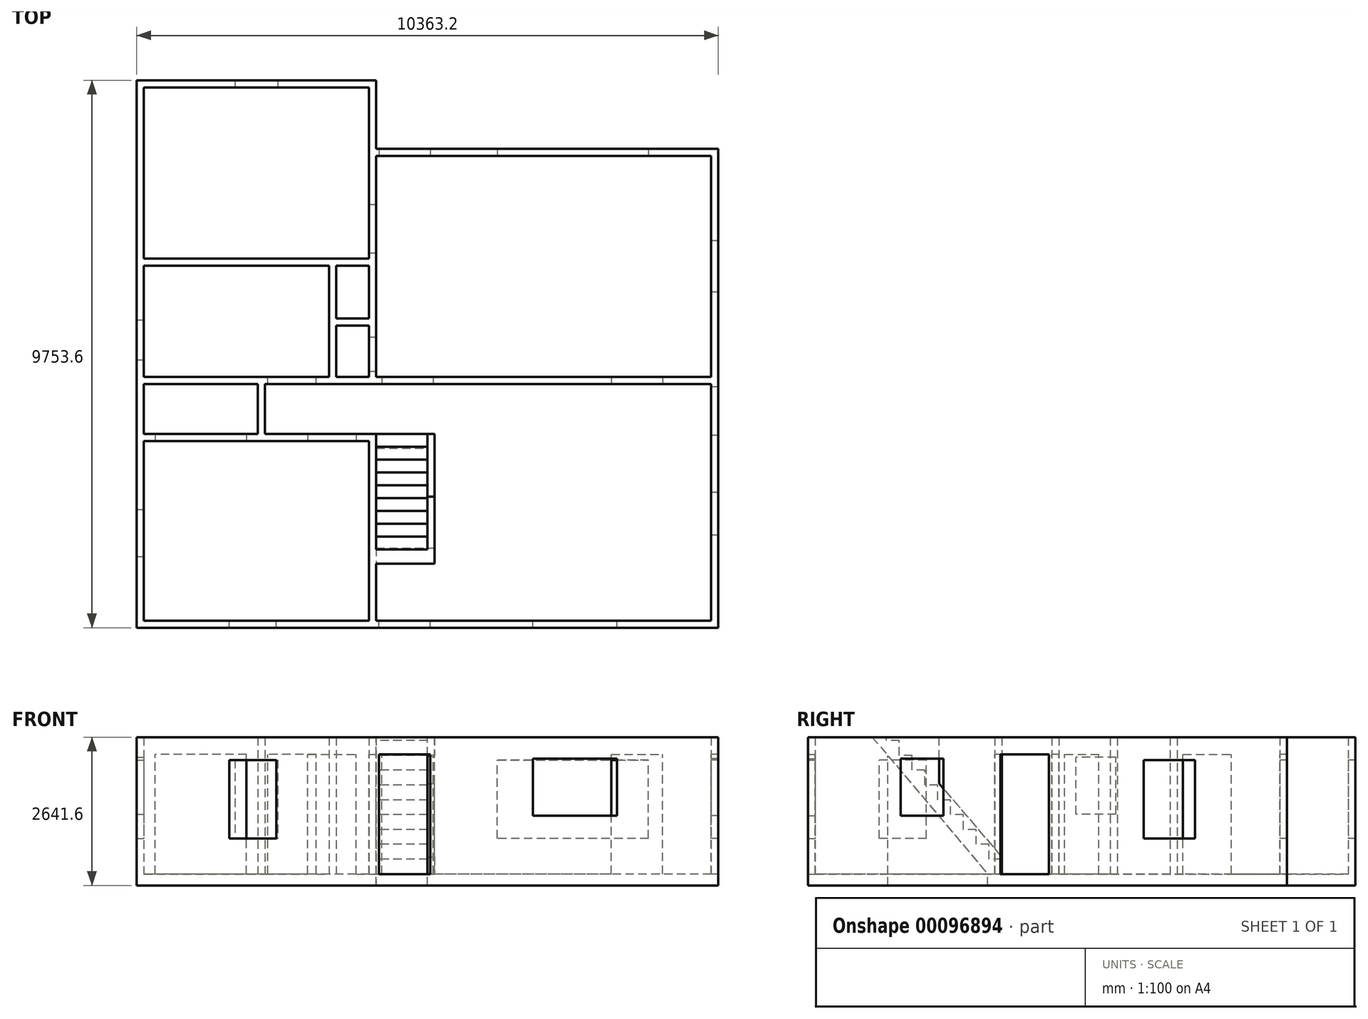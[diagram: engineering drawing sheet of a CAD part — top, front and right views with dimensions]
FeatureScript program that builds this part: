
annotation { "Feature Type Name" : "Feature", "Feature Type Description" : "" }
export const myFeature = defineFeature(function(context is Context, id is Id, definition is map)
    precondition{}
    {
        {
            var Q0;
            Q0=qCreatedBy(makeId("Top.planeOp"),FACE);
            var sketch = newSketch(context, id + "F0", { "sketchPlane" : qUnion([Q0])});
            skLineSegment(sketch, "E0", {"start": v(0, 0) * mm, "end": v(10363.2, 0) * mm});
            skLineSegment(sketch, "E1", {"start": v(10363.2, 0) * mm, "end": v(10363.2, 8534.4) * mm});
            skLineSegment(sketch, "E2", {"start": v(10363.2, 8534.4) * mm, "end": v(4267.2, 8534.4) * mm});
            skLineSegment(sketch, "E3", {"start": v(4267.2, 8534.4) * mm, "end": v(4267.2, 9753.6) * mm});
            skLineSegment(sketch, "E4", {"start": v(4267.2, 9753.6) * mm, "end": v(0, 9753.6) * mm});
            skLineSegment(sketch, "E5", {"start": v(0, 9753.6) * mm, "end": v(0, 0) * mm});
            skLineSegment(sketch, "E6", {"start": v(127, 3327.4) * mm, "end": v(127, 127) * mm});
            skLineSegment(sketch, "E7", {"start": v(127, 127) * mm, "end": v(4140.2, 127) * mm});
            skLineSegment(sketch, "E8", {"start": v(4140.2, 127) * mm, "end": v(4140.2, 3327.4) * mm});
            skLineSegment(sketch, "E9", {"start": v(4140.2, 3327.4) * mm, "end": v(127, 3327.4) * mm});
            skLineSegment(sketch, "E10", {"start": v(4267.2, 3327.4) * mm, "end": v(4267.2, 127) * mm});
            skLineSegment(sketch, "E11", {"start": v(4267.2, 127) * mm, "end": v(5181.6, 127) * mm});
            skLineSegment(sketch, "E12", {"start": v(5181.6, 127) * mm, "end": v(5181.6, 3327.4) * mm});
            skLineSegment(sketch, "E13", {"start": v(5181.6, 3327.4) * mm, "end": v(4267.2, 3327.4) * mm});
            skLineSegment(sketch, "E14", {"start": v(2286, 3454.4) * mm, "end": v(5308.6, 3454.4) * mm});
            skLineSegment(sketch, "E15", {"start": v(5308.6, 3454.4) * mm, "end": v(5308.6, 127) * mm});
            skLineSegment(sketch, "E16", {"start": v(5308.6, 127) * mm, "end": v(10236.2, 127) * mm});
            skLineSegment(sketch, "E17", {"start": v(10236.2, 127) * mm, "end": v(10236.2, 4343.4) * mm});
            skLineSegment(sketch, "E18", {"start": v(10236.2, 4343.4) * mm, "end": v(2286, 4343.4) * mm});
            skLineSegment(sketch, "E19", {"start": v(2286, 4343.4) * mm, "end": v(2286, 3454.4) * mm});
            skLineSegment(sketch, "E20", {"start": v(4267.2, 8407.4) * mm, "end": v(4267.2, 4470.4) * mm});
            skLineSegment(sketch, "E21", {"start": v(4267.2, 4470.4) * mm, "end": v(10236.2, 4470.4) * mm});
            skLineSegment(sketch, "E22", {"start": v(10236.2, 4470.4) * mm, "end": v(10236.2, 8407.4) * mm});
            skLineSegment(sketch, "E23", {"start": v(10236.2, 8407.4) * mm, "end": v(4267.2, 8407.4) * mm});
            skLineSegment(sketch, "E24", {"start": v(127, 4343.4) * mm, "end": v(127, 3454.4) * mm});
            skLineSegment(sketch, "E25", {"start": v(127, 3454.4) * mm, "end": v(2159, 3454.4) * mm});
            skLineSegment(sketch, "E26", {"start": v(2159, 3454.4) * mm, "end": v(2159, 4343.4) * mm});
            skLineSegment(sketch, "E27", {"start": v(2159, 4343.4) * mm, "end": v(127, 4343.4) * mm});
            skLineSegment(sketch, "E28", {"start": v(127, 6451.6) * mm, "end": v(127, 4470.4) * mm});
            skLineSegment(sketch, "E29", {"start": v(127, 4470.4) * mm, "end": v(3429, 4470.4) * mm});
            skLineSegment(sketch, "E30", {"start": v(3429, 4470.4) * mm, "end": v(3429, 6451.6) * mm});
            skLineSegment(sketch, "E31", {"start": v(3429, 6451.6) * mm, "end": v(127, 6451.6) * mm});
            skLineSegment(sketch, "E32", {"start": v(127, 9626.6) * mm, "end": v(127, 6578.6) * mm});
            skLineSegment(sketch, "E33", {"start": v(127, 6578.6) * mm, "end": v(4140.2, 6578.6) * mm});
            skLineSegment(sketch, "E34", {"start": v(4140.2, 6578.6) * mm, "end": v(4140.2, 9626.6) * mm});
            skLineSegment(sketch, "E35", {"start": v(4140.2, 9626.6) * mm, "end": v(127, 9626.6) * mm});
            skLineSegment(sketch, "E36", {"start": v(3556, 6451.6) * mm, "end": v(3556, 5511.8) * mm});
            skLineSegment(sketch, "E37", {"start": v(3556, 5511.8) * mm, "end": v(4140.2, 5511.8) * mm});
            skLineSegment(sketch, "E38", {"start": v(4140.2, 5511.8) * mm, "end": v(4140.2, 6451.6) * mm});
            skLineSegment(sketch, "E39", {"start": v(4140.2, 6451.6) * mm, "end": v(3556, 6451.6) * mm});
            skLineSegment(sketch, "E40", {"start": v(3556, 5384.8) * mm, "end": v(3556, 4470.4) * mm});
            skLineSegment(sketch, "E41", {"start": v(3556, 4470.4) * mm, "end": v(4140.2, 4470.4) * mm});
            skLineSegment(sketch, "E42", {"start": v(4140.2, 4470.4) * mm, "end": v(4140.2, 5384.8) * mm});
            skLineSegment(sketch, "E43", {"start": v(4140.2, 5384.8) * mm, "end": v(3556, 5384.8) * mm});
            skSolve(sketch);
        }
        {
            var Q0;
            Q0=makeQuery(id+"F0.imprint","IMPRINT",FACE,{"disambiguationData":[TD([[makeQuery(id+"F0.imprint","IMPRINT",EDGE,{"derivedFrom":sQuery(id+"F0.wireOp",EDGE,"E0")}),1.0]])]});
            extrude(context, id + "F1", {"entities" : qUnion([Q0]), "depth" : 2438.4 * mm});
        }
        {
            var Q0;
            Q0=qCreatedBy(makeId("Top.planeOp"),FACE);
            var sketch = newSketch(context, id + "F2", { "sketchPlane" : qUnion([Q0])});
            skLineSegment(sketch, "E44", {"start": v(0, 0) * mm, "end": v(10363.2, 0) * mm});
            skLineSegment(sketch, "E45", {"start": v(10363.2, 0) * mm, "end": v(10363.2, 8534.4) * mm});
            skLineSegment(sketch, "E46", {"start": v(10363.2, 8534.4) * mm, "end": v(4267.2, 8534.4) * mm});
            skLineSegment(sketch, "E47", {"start": v(4267.2, 8534.4) * mm, "end": v(4267.2, 9753.6) * mm});
            skLineSegment(sketch, "E48", {"start": v(4267.2, 9753.6) * mm, "end": v(0, 9753.6) * mm});
            skLineSegment(sketch, "E49", {"start": v(0, 9753.6) * mm, "end": v(0, 0) * mm});
            skLineSegment(sketch, "E50.bottom", {"start": v(4267.2, 3200.4) * mm, "end": v(5181.6, 3200.4) * mm});
            skLineSegment(sketch, "E50.top", {"start": v(4267.2, 1422.4) * mm, "end": v(5181.6, 1422.4) * mm});
            skLineSegment(sketch, "E50.left", {"start": v(4267.2, 3200.4) * mm, "end": v(4267.2, 1422.4) * mm});
            skLineSegment(sketch, "E50.right", {"start": v(5181.6, 3200.4) * mm, "end": v(5181.6, 1422.4) * mm});
            skSolve(sketch);
        }
        {
            var Q0;
            Q0=makeQuery(id+"F2.imprint","IMPRINT",FACE,{"disambiguationData":[TD([[makeQuery(id+"F2.imprint","IMPRINT",EDGE,{"derivedFrom":sQuery(id+"F2.wireOp",EDGE,"E44")}),1.0]])]});
            extrude(context, id + "F3", {"entities" : qUnion([Q0]), "operationType" : NewBodyOperationType.ADD, "oppositeDirection" : true, "depth" : 203.2 * mm});
        }
        {
            var Q0;
            Q0=makeQuery(id+"F1.opExtrude","SWEPT_FACE",FACE,{"disambiguationData":[OSD([sQuery(id+"F0.wireOp",EDGE,"E17")])]});
            var sketch = newSketch(context, id + "F4", { "sketchPlane" : qUnion([Q0])});
            skLineSegment(sketch, "E51.bottom", {"start": v(-4292.6, 0) * mm, "end": v(-3429, 0) * mm});
            skLineSegment(sketch, "E51.top", {"start": v(-4292.6, 2133.6) * mm, "end": v(-3429, 2133.6) * mm});
            skLineSegment(sketch, "E51.left", {"start": v(-4292.6, 0) * mm, "end": v(-4292.6, 2133.6) * mm});
            skLineSegment(sketch, "E51.right", {"start": v(-3429, 0) * mm, "end": v(-3429, 2133.6) * mm});
            skLineSegment(sketch, "E52.bottom", {"start": v(-2413, 2057.4) * mm, "end": v(-1651, 2057.4) * mm});
            skLineSegment(sketch, "E52.top", {"start": v(-2413, 1041.4) * mm, "end": v(-1651, 1041.4) * mm});
            skLineSegment(sketch, "E52.left", {"start": v(-2413, 2057.4) * mm, "end": v(-2413, 1041.4) * mm});
            skLineSegment(sketch, "E52.right", {"start": v(-1651, 2057.4) * mm, "end": v(-1651, 1041.4) * mm});
            skSolve(sketch);
        }
        {
            var Q0;
            Q0 = qSketchRegion(id + "F4", true);
            extrude(context, id + "F5", {"entities" : qUnion([Q0]), "operationType" : NewBodyOperationType.REMOVE, "endBound" : BoundingType.UP_TO_NEXT, "oppositeDirection" : true, "depth" : 25.4 * mm});
        }
        {
            var Q0;
            Q0=makeQuery(id+"F1.opExtrude","SWEPT_FACE",FACE,{"disambiguationData":[OSD([sQuery(id+"F0.wireOp",EDGE,"E18")])]});
            var sketch = newSketch(context, id + "F6", { "sketchPlane" : qUnion([Q0])});
            skLineSegment(sketch, "E53.bottom", {"start": v(4368.8, 0) * mm, "end": v(5283.2, 0) * mm});
            skLineSegment(sketch, "E53.top", {"start": v(4368.8, 2133.6) * mm, "end": v(5283.2, 2133.6) * mm});
            skLineSegment(sketch, "E53.left", {"start": v(5283.2, 0) * mm, "end": v(5283.2, 2133.6) * mm});
            skLineSegment(sketch, "E53.right", {"start": v(4368.8, 0) * mm, "end": v(4368.8, 2133.6) * mm});
            skLineSegment(sketch, "E54.bottom", {"start": v(8458.2, 0) * mm, "end": v(9372.6, 0) * mm});
            skLineSegment(sketch, "E54.top", {"start": v(8458.2, 2133.6) * mm, "end": v(9372.6, 2133.6) * mm});
            skLineSegment(sketch, "E54.left", {"start": v(8458.2, 0) * mm, "end": v(8458.2, 2133.6) * mm});
            skLineSegment(sketch, "E54.right", {"start": v(9372.6, 0) * mm, "end": v(9372.6, 2133.6) * mm});
            skSolve(sketch);
        }
        {
            var Q0;
            Q0 = qSketchRegion(id + "F6", true);
            extrude(context, id + "F7", {"entities" : qUnion([Q0]), "operationType" : NewBodyOperationType.REMOVE, "endBound" : BoundingType.UP_TO_NEXT, "oppositeDirection" : true, "depth" : 25.4 * mm});
        }
        {
            var Q0;
            Q0=makeQuery(id+"F1.opExtrude","SWEPT_FACE",FACE,{"disambiguationData":[OSD([sQuery(id+"F0.wireOp",EDGE,"E15")])]});
            var sketch = newSketch(context, id + "F8", { "sketchPlane" : qUnion([Q0])});
            skLineSegment(sketch, "E55.bottom", {"start": v(127, 0) * mm, "end": v(1422.4, 0) * mm});
            skLineSegment(sketch, "E55.left", {"start": v(127, 0) * mm, "end": v(127, 2438.4) * mm});
            skLineSegment(sketch, "E55.right", {"start": v(1422.4, 0) * mm, "end": v(1422.4, 2107.26) * mm});
            skLineSegment(sketch, "E56", {"start": v(1143, 2438.4) * mm, "end": v(127, 2438.4) * mm});
            skLineSegment(sketch, "E57", {"start": v(1143, 2438.4) * mm, "end": v(1422.4, 2107.26) * mm});
            skSolve(sketch);
        }
        {
            var Q0;
            Q0 = qSketchRegion(id + "F8", true);
            extrude(context, id + "F9", {"entities" : qUnion([Q0]), "operationType" : NewBodyOperationType.REMOVE, "endBound" : BoundingType.UP_TO_NEXT, "oppositeDirection" : true, "depth" : 25.4 * mm});
        }
        {
            var Q0;
            Q0=makeQuery(id+"F9.boolean.opBoolean","MERGE",FACE,{"derivedFrom":[makeQuery(id+"F1.opExtrude","SWEPT_FACE",FACE,{"disambiguationData":[OSD([sQuery(id+"F0.wireOp",EDGE,"E11")])]}),makeQuery(id+"F1.opExtrude","SWEPT_FACE",FACE,{"disambiguationData":[OSD([sQuery(id+"F0.wireOp",EDGE,"E16")])]}),makeQuery(id+"F9.opExtrude","SWEPT_FACE",FACE,{"disambiguationData":[OSD([sQuery(id+"F8.wireOp",EDGE,"E55.left")])]})]});
            var sketch = newSketch(context, id + "F10", { "sketchPlane" : qUnion([Q0])});
            skLineSegment(sketch, "E58.bottom", {"start": v(-8559.8, 2057.4) * mm, "end": v(-7061.2, 2057.4) * mm});
            skLineSegment(sketch, "E58.top", {"start": v(-8559.8, 1041.4) * mm, "end": v(-7061.2, 1041.4) * mm});
            skLineSegment(sketch, "E58.left", {"start": v(-8559.8, 2057.4) * mm, "end": v(-8559.8, 1041.4) * mm});
            skLineSegment(sketch, "E58.right", {"start": v(-7061.2, 2057.4) * mm, "end": v(-7061.2, 1041.4) * mm});
            skLineSegment(sketch, "E59.bottom", {"start": v(-5232.4, 0) * mm, "end": v(-4318, 0) * mm});
            skLineSegment(sketch, "E59.top", {"start": v(-5232.4, 2133.6) * mm, "end": v(-4318, 2133.6) * mm});
            skLineSegment(sketch, "E59.left", {"start": v(-5232.4, 0) * mm, "end": v(-5232.4, 2133.6) * mm});
            skLineSegment(sketch, "E59.right", {"start": v(-4318, 0) * mm, "end": v(-4318, 2133.6) * mm});
            skSolve(sketch);
        }
        {
            var Q0;
            Q0 = qSketchRegion(id + "F10", true);
            extrude(context, id + "F11", {"entities" : qUnion([Q0]), "operationType" : NewBodyOperationType.REMOVE, "endBound" : BoundingType.UP_TO_NEXT, "oppositeDirection" : true, "depth" : 25.4 * mm});
        }
        {
            var Q0;
            Q0=makeQuery(id+"F1.opExtrude","SWEPT_FACE",FACE,{"disambiguationData":[OSD([sQuery(id+"F0.wireOp",EDGE,"E22")])]});
            var sketch = newSketch(context, id + "F12", { "sketchPlane" : qUnion([Q0])});
            skLineSegment(sketch, "E60.bottom", {"start": v(-6896.1, 635) * mm, "end": v(-5981.7, 635) * mm});
            skLineSegment(sketch, "E60.top", {"start": v(-6896.1, 2032) * mm, "end": v(-5981.7, 2032) * mm});
            skLineSegment(sketch, "E60.left", {"start": v(-6896.1, 635) * mm, "end": v(-6896.1, 2032) * mm});
            skLineSegment(sketch, "E60.right", {"start": v(-5981.7, 635) * mm, "end": v(-5981.7, 2032) * mm});
            skSolve(sketch);
        }
        {
            var Q0;
            Q0 = qSketchRegion(id + "F12", true);
            extrude(context, id + "F13", {"entities" : qUnion([Q0]), "operationType" : NewBodyOperationType.REMOVE, "endBound" : BoundingType.UP_TO_NEXT, "oppositeDirection" : true, "depth" : 25.4 * mm});
        }
        {
            var Q0;
            Q0=makeQuery(id+"F1.opExtrude","SWEPT_FACE",FACE,{"disambiguationData":[OSD([sQuery(id+"F0.wireOp",EDGE,"E23")])]});
            var sketch = newSketch(context, id + "F14", { "sketchPlane" : qUnion([Q0])});
            skLineSegment(sketch, "E61.bottom", {"start": v(4318, 0) * mm, "end": v(5232.4, 0) * mm});
            skLineSegment(sketch, "E61.top", {"start": v(4318, 2133.6) * mm, "end": v(5232.4, 2133.6) * mm});
            skLineSegment(sketch, "E61.left", {"start": v(4318, 0) * mm, "end": v(4318, 2133.6) * mm});
            skLineSegment(sketch, "E61.right", {"start": v(5232.4, 0) * mm, "end": v(5232.4, 2133.6) * mm});
            skLineSegment(sketch, "E62.bottom", {"start": v(6426.2, 2032) * mm, "end": v(9118.6, 2032) * mm});
            skLineSegment(sketch, "E62.top", {"start": v(6426.2, 635) * mm, "end": v(9118.6, 635) * mm});
            skLineSegment(sketch, "E62.left", {"start": v(6426.2, 2032) * mm, "end": v(6426.2, 635) * mm});
            skLineSegment(sketch, "E62.right", {"start": v(9118.6, 2032) * mm, "end": v(9118.6, 635) * mm});
            skSolve(sketch);
        }
        {
            var Q0;
            Q0 = qSketchRegion(id + "F14", true);
            extrude(context, id + "F15", {"entities" : qUnion([Q0]), "operationType" : NewBodyOperationType.REMOVE, "endBound" : BoundingType.UP_TO_NEXT, "oppositeDirection" : true, "depth" : 25.4 * mm, "hasSecondDirection" : true, "secondDirectionOppositeDirection" : false, "secondDirectionDepth" : 25.4 * mm});
        }
        {
            var Q0;
            Q0=makeQuery(id+"F1.opExtrude","SWEPT_FACE",FACE,{"disambiguationData":[OSD([sQuery(id+"F0.wireOp",EDGE,"E20")])]});
            var sketch = newSketch(context, id + "F16", { "sketchPlane" : qUnion([Q0])});
            skLineSegment(sketch, "E63.bottom", {"start": v(4572, 0) * mm, "end": v(5181.6, 0) * mm});
            skLineSegment(sketch, "E63.top", {"start": v(4572, 2133.6) * mm, "end": v(5181.6, 2133.6) * mm});
            skLineSegment(sketch, "E63.left", {"start": v(4572, 0) * mm, "end": v(4572, 2133.6) * mm});
            skLineSegment(sketch, "E63.right", {"start": v(5181.6, 0) * mm, "end": v(5181.6, 2133.6) * mm});
            skLineSegment(sketch, "E64.bottom", {"start": v(6680.2, 0) * mm, "end": v(7543.8, 0) * mm});
            skLineSegment(sketch, "E64.top", {"start": v(6680.2, 2133.6) * mm, "end": v(7543.8, 2133.6) * mm});
            skLineSegment(sketch, "E64.left", {"start": v(6680.2, 0) * mm, "end": v(6680.2, 2133.6) * mm});
            skLineSegment(sketch, "E64.right", {"start": v(7543.8, 0) * mm, "end": v(7543.8, 2133.6) * mm});
            skSolve(sketch);
        }
        {
            var Q0;
            Q0 = qSketchRegion(id + "F16", true);
            extrude(context, id + "F17", {"entities" : qUnion([Q0]), "operationType" : NewBodyOperationType.REMOVE, "endBound" : BoundingType.UP_TO_NEXT, "oppositeDirection" : true, "depth" : 25.4 * mm});
        }
        {
            var Q0;
            Q0=makeQuery(id+"F1.opExtrude","SWEPT_FACE",FACE,{"disambiguationData":[OSD([sQuery(id+"F0.wireOp",EDGE,"E28")])]});
            var sketch = newSketch(context, id + "F18", { "sketchPlane" : qUnion([Q0])});
            skLineSegment(sketch, "E65.bottom", {"start": v(4775.2, 2082.8) * mm, "end": v(5486.4, 2082.8) * mm});
            skLineSegment(sketch, "E65.top", {"start": v(4775.2, 1066.8) * mm, "end": v(5486.4, 1066.8) * mm});
            skLineSegment(sketch, "E65.left", {"start": v(4775.2, 2082.8) * mm, "end": v(4775.2, 1066.8) * mm});
            skLineSegment(sketch, "E65.right", {"start": v(5486.4, 2082.8) * mm, "end": v(5486.4, 1066.8) * mm});
            skSolve(sketch);
        }
        {
            var Q0;
            Q0 = qSketchRegion(id + "F18", true);
            extrude(context, id + "F19", {"entities" : qUnion([Q0]), "operationType" : NewBodyOperationType.REMOVE, "endBound" : BoundingType.UP_TO_NEXT, "oppositeDirection" : true, "depth" : 25.4 * mm});
        }
        {
            var Q0;
            Q0=makeQuery(id+"F1.opExtrude","SWEPT_FACE",FACE,{"disambiguationData":[OSD([sQuery(id+"F0.wireOp",EDGE,"E29")])]});
            var sketch = newSketch(context, id + "F20", { "sketchPlane" : qUnion([Q0])});
            skLineSegment(sketch, "E66.bottom", {"start": v(-3200.4, 0) * mm, "end": v(-2336.8, 0) * mm});
            skLineSegment(sketch, "E66.top", {"start": v(-3200.4, 2133.6) * mm, "end": v(-2336.8, 2133.6) * mm});
            skLineSegment(sketch, "E66.left", {"start": v(-3200.4, 0) * mm, "end": v(-3200.4, 2133.6) * mm});
            skLineSegment(sketch, "E66.right", {"start": v(-2336.8, 0) * mm, "end": v(-2336.8, 2133.6) * mm});
            skSolve(sketch);
        }
        {
            var Q0;
            Q0 = qSketchRegion(id + "F20", true);
            extrude(context, id + "F21", {"entities" : qUnion([Q0]), "operationType" : NewBodyOperationType.REMOVE, "endBound" : BoundingType.UP_TO_NEXT, "oppositeDirection" : true, "depth" : 25.4 * mm});
        }
        {
            var Q0;
            Q0=makeQuery(id+"F1.opExtrude","SWEPT_FACE",FACE,{"disambiguationData":[OSD([sQuery(id+"F0.wireOp",EDGE,"E9")])]});
            var sketch = newSketch(context, id + "F22", { "sketchPlane" : qUnion([Q0])});
            skLineSegment(sketch, "E67.bottom", {"start": v(3048, 0) * mm, "end": v(3911.6, 0) * mm});
            skLineSegment(sketch, "E67.top", {"start": v(3048, 2133.6) * mm, "end": v(3911.6, 2133.6) * mm});
            skLineSegment(sketch, "E67.left", {"start": v(3048, 0) * mm, "end": v(3048, 2133.6) * mm});
            skLineSegment(sketch, "E67.right", {"start": v(3911.6, 0) * mm, "end": v(3911.6, 2133.6) * mm});
            skLineSegment(sketch, "E68.bottom", {"start": v(1955.8, 0) * mm, "end": v(330.2, 0) * mm});
            skLineSegment(sketch, "E68.top", {"start": v(1955.8, 2133.6) * mm, "end": v(330.2, 2133.6) * mm});
            skLineSegment(sketch, "E68.left", {"start": v(1955.8, 0) * mm, "end": v(1955.8, 2133.6) * mm});
            skLineSegment(sketch, "E68.right", {"start": v(330.2, 0) * mm, "end": v(330.2, 2133.6) * mm});
            skSolve(sketch);
        }
        {
            var Q0;
            Q0 = qSketchRegion(id + "F22", true);
            extrude(context, id + "F23", {"entities" : qUnion([Q0]), "operationType" : NewBodyOperationType.REMOVE, "endBound" : BoundingType.UP_TO_NEXT, "oppositeDirection" : true, "depth" : 25.4 * mm});
        }
        {
            var Q0;
            Q0=makeQuery(id+"F1.opExtrude","SWEPT_FACE",FACE,{"disambiguationData":[OSD([sQuery(id+"F0.wireOp",EDGE,"E6")])]});
            var sketch = newSketch(context, id + "F24", { "sketchPlane" : qUnion([Q0])});
            skLineSegment(sketch, "E69.bottom", {"start": v(1270, 2032) * mm, "end": v(2108.2, 2032) * mm});
            skLineSegment(sketch, "E69.top", {"start": v(1270, 635) * mm, "end": v(2108.2, 635) * mm});
            skLineSegment(sketch, "E69.left", {"start": v(1270, 2032) * mm, "end": v(1270, 635) * mm});
            skLineSegment(sketch, "E69.right", {"start": v(2108.2, 2032) * mm, "end": v(2108.2, 635) * mm});
            skSolve(sketch);
        }
        {
            var Q0;
            Q0 = qSketchRegion(id + "F24", true);
            extrude(context, id + "F25", {"entities" : qUnion([Q0]), "operationType" : NewBodyOperationType.REMOVE, "endBound" : BoundingType.UP_TO_NEXT, "oppositeDirection" : true, "depth" : 25.4 * mm});
        }
        {
            var Q0;
            Q0=makeQuery(id+"F1.opExtrude","SWEPT_FACE",FACE,{"disambiguationData":[OSD([sQuery(id+"F0.wireOp",EDGE,"E7")])]});
            var sketch = newSketch(context, id + "F26", { "sketchPlane" : qUnion([Q0])});
            skLineSegment(sketch, "E70.bottom", {"start": v(-1651, 2032) * mm, "end": v(-2489.2, 2032) * mm});
            skLineSegment(sketch, "E70.top", {"start": v(-1651, 635) * mm, "end": v(-2489.2, 635) * mm});
            skLineSegment(sketch, "E70.left", {"start": v(-1651, 2032) * mm, "end": v(-1651, 635) * mm});
            skLineSegment(sketch, "E70.right", {"start": v(-2489.2, 2032) * mm, "end": v(-2489.2, 635) * mm});
            skSolve(sketch);
        }
        {
            var Q0;
            Q0 = qSketchRegion(id + "F26", true);
            extrude(context, id + "F27", {"entities" : qUnion([Q0]), "operationType" : NewBodyOperationType.REMOVE, "endBound" : BoundingType.UP_TO_NEXT, "oppositeDirection" : true, "depth" : 25.4 * mm});
        }
        {
            var Q0;
            Q0=makeQuery(id+"F1.opExtrude","SWEPT_FACE",FACE,{"disambiguationData":[OSD([sQuery(id+"F0.wireOp",EDGE,"E13")])]});
            var sketch = newSketch(context, id + "F28", { "sketchPlane" : qUnion([Q0])});
            skLineSegment(sketch, "E71.bottom", {"start": v(4267.2, 0) * mm, "end": v(5181.6, 0) * mm});
            skLineSegment(sketch, "E71.top", {"start": v(4267.2, 2438.4) * mm, "end": v(5181.6, 2438.4) * mm});
            skLineSegment(sketch, "E71.left", {"start": v(4267.2, 0) * mm, "end": v(4267.2, 2438.4) * mm});
            skLineSegment(sketch, "E71.right", {"start": v(5181.6, 0) * mm, "end": v(5181.6, 2438.4) * mm});
            skSolve(sketch);
        }
        {
            var Q0;
            Q0 = qSketchRegion(id + "F28", true);
            extrude(context, id + "F29", {"entities" : qUnion([Q0]), "operationType" : NewBodyOperationType.REMOVE, "endBound" : BoundingType.UP_TO_NEXT, "oppositeDirection" : true, "depth" : 25.4 * mm});
        }
        {
            var Q0;
            Q0=makeQuery(id+"F29.boolean.opBoolean","MERGE",FACE,{"derivedFrom":[makeQuery(id+"F3.boolean.opBoolean","MERGE",FACE,{"derivedFrom":[makeQuery(id+"F1.opExtrude","SWEPT_FACE",FACE,{"disambiguationData":[OSD([sQuery(id+"F0.wireOp",EDGE,"E10")])]}),makeQuery(id+"F3.opExtrude","SWEPT_FACE",FACE,{"disambiguationData":[OSD([sQuery(id+"F2.wireOp",EDGE,"E50.left")])]})]}),makeQuery(id+"F29.opExtrude","SWEPT_FACE",FACE,{"disambiguationData":[OSD([sQuery(id+"F28.wireOp",EDGE,"E71.left")])]})]});
            var sketch = newSketch(context, id + "F34", { "sketchPlane" : qUnion([Q0])});
            skLineSegment(sketch, "E72", {"start": v(3454.4, 0) * mm, "end": v(3454.4, 264.16) * mm});
            skLineSegment(sketch, "E73", {"start": v(3454.4, 264.16) * mm, "end": v(3225.8, 264.16) * mm});
            skLineSegment(sketch, "E74", {"start": v(3225.8, 264.16) * mm, "end": v(3225.8, 528.32) * mm});
            skLineSegment(sketch, "E75", {"start": v(3454.4, 0) * mm, "end": v(3200.4, 0) * mm});
            skLineSegment(sketch, "E76", {"start": v(3225.8, 528.32) * mm, "end": v(2997.2, 528.32) * mm});
            skLineSegment(sketch, "E77", {"start": v(2997.2, 528.32) * mm, "end": v(2997.2, 792.48) * mm});
            skLineSegment(sketch, "E78", {"start": v(2997.2, 792.48) * mm, "end": v(2768.6, 792.48) * mm});
            skLineSegment(sketch, "E79", {"start": v(2768.6, 792.48) * mm, "end": v(2768.6, 1056.64) * mm});
            skLineSegment(sketch, "E80", {"start": v(2768.6, 1056.64) * mm, "end": v(2540, 1056.64) * mm});
            skLineSegment(sketch, "E81", {"start": v(2540, 1056.64) * mm, "end": v(2540, 1320.8) * mm});
            skLineSegment(sketch, "E82", {"start": v(2540, 1320.8) * mm, "end": v(2311.4, 1320.8) * mm});
            skLineSegment(sketch, "E83", {"start": v(2311.4, 1320.8) * mm, "end": v(2311.4, 1584.96) * mm});
            skLineSegment(sketch, "E84", {"start": v(2311.4, 1584.96) * mm, "end": v(2082.8, 1584.96) * mm});
            skLineSegment(sketch, "E85", {"start": v(2082.8, 1584.96) * mm, "end": v(2082.8, 1849.12) * mm});
            skLineSegment(sketch, "E86", {"start": v(2082.8, 1849.12) * mm, "end": v(1854.2, 1849.12) * mm});
            skLineSegment(sketch, "E87", {"start": v(1854.2, 1849.12) * mm, "end": v(1854.2, 2113.28) * mm});
            skLineSegment(sketch, "E88", {"start": v(1854.2, 2113.28) * mm, "end": v(1625.6, 2113.28) * mm});
            skLineSegment(sketch, "E89", {"start": v(1625.6, 2113.28) * mm, "end": v(1625.6, 2377.44) * mm});
            skLineSegment(sketch, "E90", {"start": v(1625.6, 2377.44) * mm, "end": v(1397, 2377.44) * mm});
            skLineSegment(sketch, "E91", {"start": v(1397, 2377.44) * mm, "end": v(1397, 2438.4) * mm});
            skLineSegment(sketch, "E92", {"start": v(1397, 2438.4) * mm, "end": v(1143, 2438.4) * mm});
            skLineSegment(sketch, "E93", {"start": v(1143, 2438.4) * mm, "end": v(3200.4, 0) * mm});
            skSolve(sketch);
        }
        {
            var Q0;
            Q0 = qSketchRegion(id + "F34", true);
            extrude(context, id + "F35", {"entities" : qUnion([Q0]), "operationType" : NewBodyOperationType.ADD, "depth" : 914.4 * mm});
        }
        {
            var Q0;
            Q0=makeQuery(id+"F1.opExtrude","SWEPT_FACE",FACE,{"disambiguationData":[OSD([sQuery(id+"F0.wireOp",EDGE,"E15")])]});
            var sketch = newSketch(context, id + "F30", { "sketchPlane" : qUnion([Q0])});
            skLineSegment(sketch, "E94", {"start": v(3454.4, 304.8) * mm, "end": v(2336.8, 1612.9) * mm});
            skLineSegment(sketch, "E95", {"start": v(2336.8, 1612.9) * mm, "end": v(2336.8, 2438.4) * mm});
            skLineSegment(sketch, "E96", {"start": v(2336.8, 2438.4) * mm, "end": v(3454.4, 2438.4) * mm});
            skLineSegment(sketch, "E97", {"start": v(3454.4, 2438.4) * mm, "end": v(3454.4, 304.8) * mm});
            skSolve(sketch);
        }
        {
            var Q0;
            Q0 = qSketchRegion(id + "F30", true);
            extrude(context, id + "F31", {"entities" : qUnion([Q0]), "operationType" : NewBodyOperationType.REMOVE, "endBound" : BoundingType.UP_TO_NEXT, "oppositeDirection" : true, "depth" : 25.4 * mm});
        }
        {
            var Q0;
            Q0=makeQuery(id+"F1.opExtrude","SWEPT_FACE",FACE,{"disambiguationData":[OSD([sQuery(id+"F0.wireOp",EDGE,"E35")])]});
            var sketch = newSketch(context, id + "F32", { "sketchPlane" : qUnion([Q0])});
            skLineSegment(sketch, "E98.bottom", {"start": v(1752.6, 2032) * mm, "end": v(2514.6, 2032) * mm});
            skLineSegment(sketch, "E98.top", {"start": v(1752.6, 635) * mm, "end": v(2514.6, 635) * mm});
            skLineSegment(sketch, "E98.left", {"start": v(1752.6, 2032) * mm, "end": v(1752.6, 635) * mm});
            skLineSegment(sketch, "E98.right", {"start": v(2514.6, 2032) * mm, "end": v(2514.6, 635) * mm});
            skSolve(sketch);
        }
        {
            var Q0;
            Q0 = qSketchRegion(id + "F32", true);
            extrude(context, id + "F33", {"entities" : qUnion([Q0]), "operationType" : NewBodyOperationType.REMOVE, "endBound" : BoundingType.UP_TO_NEXT, "oppositeDirection" : true, "depth" : 25.4 * mm});
        }
    });
